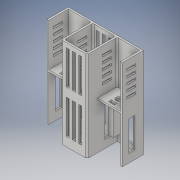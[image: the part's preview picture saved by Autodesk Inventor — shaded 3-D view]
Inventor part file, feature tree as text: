
AUTODESK INVENTOR PART (.ipt)
format: ipt  version: 2018.2 (Build 222227000, 227)  size: 435,200 bytes
history: native  units: in
note: dims shown in document units (in); Inventor stores cm internally (conversion verified against a paired STEP export)
features: sketch x12, extrude x11, fillet x8, chamfer x1
ambient origin geometry x8: Origin, YZ Plane, XZ Plane, XY Plane, X Axis, Y Axis, Z Axis, Center Point
bodies: Solid1 (feature_tree)
feature tree (32):
  extrude  "Extrusion1"  Depth=4.7244in
  extrude  "Extrusion2"  Depth=0.0945in
  extrude  "Extrusion3"  Depth=1.0236in TaperAngle=0.0deg
  extrude  "Extrusion4"  Depth=0.0945in
  extrude  "Extrusion5"  Depth=0.5906in
  extrude  "Extrusion6"  Depth=0.0945in
  extrude  "Extrusion8"  Depth=1.0236in TaperAngle=0.0deg
  extrude  "Extrusion9"  Depth=0.1575in
  fillet  "Fillet3"  Radius=0.5118in
  fillet  "Fillet4"  Radius=0.5118in
  fillet  "Fillet5"  Radius=0.5945in
  fillet  "Fillet6"  Radius=0.5945in
  fillet  "Fillet7"  Radius=0.1575in
  fillet  "Fillet8"  Radius=0.1575in
  sketch  "Sketch14"  dims[d26=0.315in]
  chamfer  "Chamfer1"  Distance=0.315in
  extrude  "Extrusion14"  Depth=0.1575in
  extrude  "Extrusion15"  Depth=0.2362in
  fillet  "Fillet11"  Radius=0.437in
  fillet  "Fillet12"  Radius=0.2362in
  extrude  "Extrusion16"  Depth=0.437in
  sketch  "Sketch1"  dims[d0=3.937in d1=4.7244in]
  sketch  "Sketch2"  dims[d2=0.0945in d3=0.0in d4=0.0945in]
  sketch  "Sketch3"  dims[d5=0.0945in d6=1.0236in d7=0.0in]
  sketch  "Sketch4"  dims[d8=0.0945in d9=0.0945in]
  sketch  "Sketch5"  dims[d10=0.5906in d11=0.5906in]
  sketch  "Sketch6"  dims[d12=1.5748in d13=0.0in d14=0.0945in]
  sketch  "Sketch8"  dims[d15=2.2441in d16=1.0236in d17=0.0in]
  sketch  "Sketch9"  dims[d18=0.2953in d19=0.2953in d20=0.5118in d21=0.5118in d22=0.5945in d23=0.5945in d24=0.1575in d25=0.1575in]
  sketch  "Sketch15"  dims[d27=0.315in]
  sketch  "Sketch16"  dims[d28=0.315in]
  sketch  "Sketch17"  dims[d29=0.1575in d30=0.315in d31=0.1575in d32=0.2362in d33=0.437in d34=0.2362in d35=0.437in d36=0.2362in d37=0.437in d38=0.437in d39=0.0945in d40=0.0in d41=0.0945in d42=1.2756in d43=0.0in d52=0.8661in d54=0.8661in d58=0.0945in d59=0.0in d64=1.5748in d65=0.315in d66=4.7244in d67=0.0in d80=0.0787in d81=0.0787in d82=0.0787in d83=0.0787in d84=0.0787in d85=0.0787in d86=0.0787in d87=0.0787in d88=45.0deg d92=0.4724in d93=0.1181in d94=0.4724in d95=0.1181in d96=0.1181in d97=0.1181in d98=0.4724in d99=0.1181in d100=0.1969in d101=0.1969in d102=0.1969in d103=0.1969in d104=4.7244in d105=0.0in d107=1.7717in d108=0.1575in d109=1.7717in d110=0.1575in d111=1.7717in d112=1.7717in d113=0.1575in d114=0.1575in d115=0.1575in d116=0.1969in d117=0.1969in d118=0.1969in d119=0.1969in d120=0.1575in d121=0.1575in d122=0.4724in d123=0.4724in d124=0.4724in d125=0.1575in d126=4.7244in d127=0.0in d130=0.0787in d131=0.0787in d132=0.4724in d133=1.5748in d134=1.5748in d135=0.3543in d136=0.0in]
